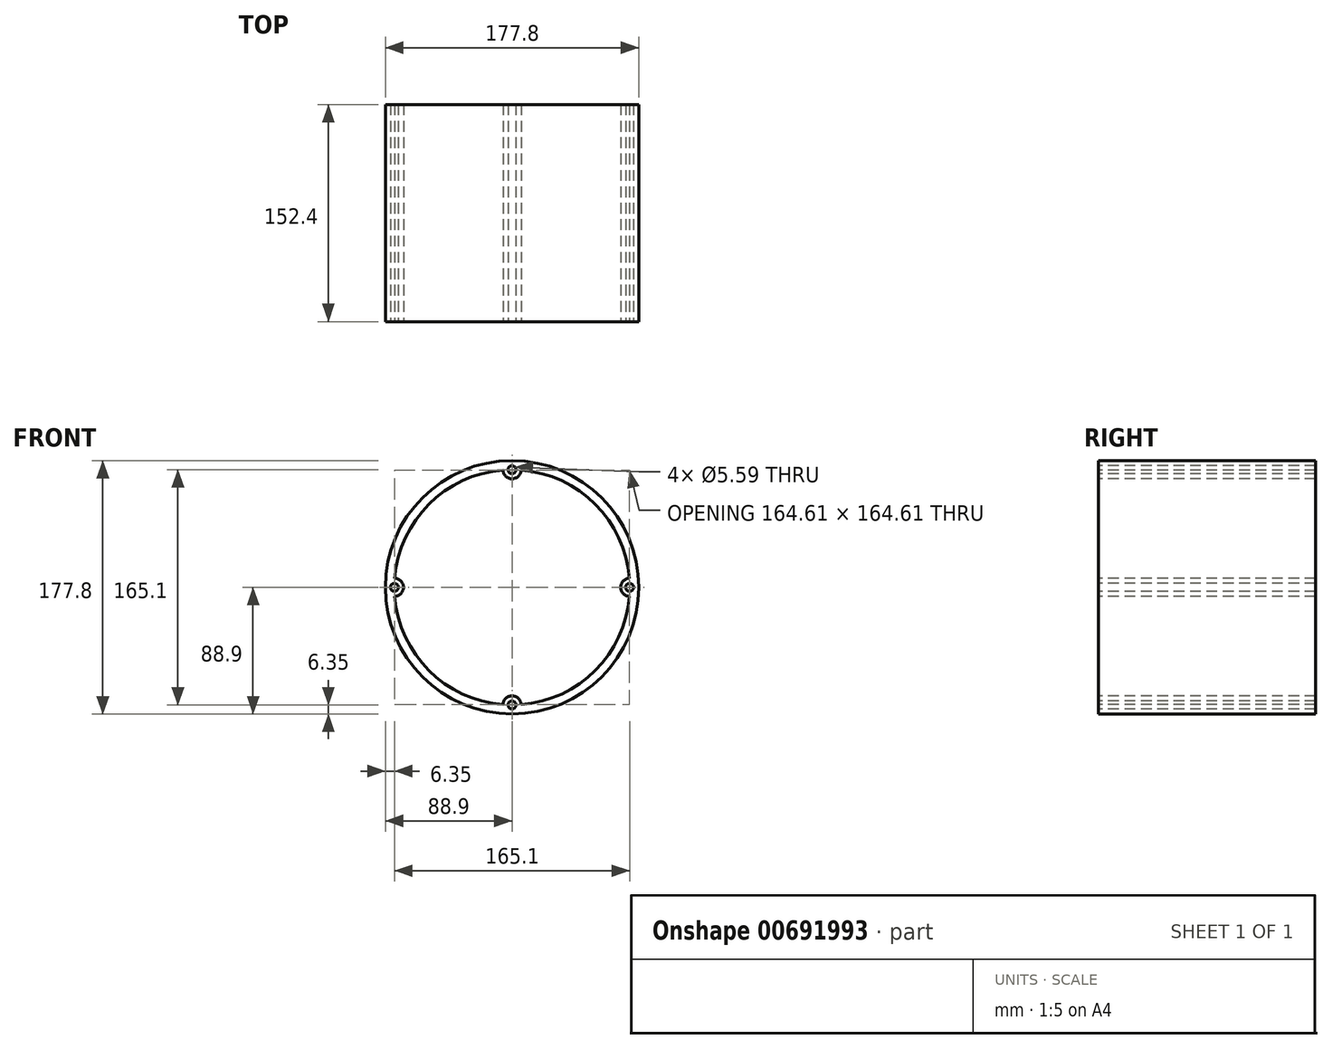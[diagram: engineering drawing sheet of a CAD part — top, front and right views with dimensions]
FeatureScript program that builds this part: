
annotation { "Feature Type Name" : "Feature", "Feature Type Description" : "" }
export const myFeature = defineFeature(function(context is Context, id is Id, definition is map)
    precondition{}
    {
        {
            var Q0;
            Q0=qCreatedBy(makeId("Front.planeOp"),FACE);
            var sketch = newSketch(context, id + "F0", { "sketchPlane" : qUnion([Q0])});
            skCircle(sketch, "E0", {"center": v(0, 0) * mm, "radius": 88.9 * mm});
            skSolve(sketch);
        }
        {
            var Q0;
            Q0=makeQuery(id+"F0.imprint","IMPRINT",FACE,{"disambiguationData":[TD([[makeQuery(id+"F0.imprint","IMPRINT",EDGE,{"derivedFrom":sQuery(id+"F0.wireOp",EDGE,"E0")}),1.0]])]});
            extrude(context, id + "F1", {"entities" : qUnion([Q0]), "oppositeDirection" : true, "depth" : 152.4 * mm, "offsetDistance" : 25.4 * mm});
        }
        {
            var Q0;
            Q0=makeQuery(id+"F1.opExtrude","CAP_FACE",FACE,{"disambiguationData":[OSD([sQuery(id+"F0.wireOp",EDGE,"E0")])],"isStart":true});
            var sketch = newSketch(context, id + "F2", { "sketchPlane" : qUnion([Q0])});
            skArc(sketch, "E1", {"start": v(2.8, -82.5) * mm, "mid": v(58.37, -58.37) * mm, "end": v(82.5, -2.8) * mm});
            skLineSegment(sketch, "E2", {"start": v(0, 0) * mm, "end": v(0, 79.76) * mm});
            skLineSegment(sketch, "E3", {"start": v(0, 0) * mm, "end": v(0, -79.76) * mm});
            skLineSegment(sketch, "E4", {"start": v(0, 0) * mm, "end": v(79.76, 0) * mm});
            skLineSegment(sketch, "E5", {"start": v(0, 0) * mm, "end": v(-79.76, 0) * mm});
            skCircle(sketch, "E6", {"center": v(0, 82.55) * mm, "radius": 2.8 * mm});
            skCircle(sketch, "E7", {"center": v(-82.55, 0) * mm, "radius": 2.8 * mm});
            skCircle(sketch, "E8", {"center": v(82.55, 0) * mm, "radius": 2.8 * mm});
            skCircle(sketch, "E9", {"center": v(0, -82.55) * mm, "radius": 2.8 * mm});
            skArc(sketch, "E10.trimOffspring", {"start": v(82.5, 2.8) * mm, "mid": v(58.37, 58.37) * mm, "end": v(2.8, 82.5) * mm});
            skArc(sketch, "E11.trimOffspring", {"start": v(-2.8, 82.5) * mm, "mid": v(-58.37, 58.37) * mm, "end": v(-82.5, 2.8) * mm});
            skArc(sketch, "E12.trimOffspring", {"start": v(-82.5, -2.8) * mm, "mid": v(-58.37, -58.37) * mm, "end": v(-2.8, -82.5) * mm});
            skSolve(sketch);
        }
        {
            var Q0;
            Q0=makeQuery(id+"F0.imprint","IMPRINT",FACE,{"disambiguationData":[TD([[makeQuery(id+"F0.imprint","IMPRINT",EDGE,{"derivedFrom":sQuery(id+"F0.wireOp",EDGE,"E0")}),1.0]])]});
            var sketch = newSketch(context, id + "F3", { "sketchPlane" : qUnion([Q0])});
            skCircle(sketch, "E13", {"center": v(0, 82.55) * mm, "radius": 6.35 * mm});
            skCircle(sketch, "E14", {"center": v(82.55, 0) * mm, "radius": 6.35 * mm});
            skCircle(sketch, "E15", {"center": v(-82.55, 0) * mm, "radius": 6.35 * mm});
            skCircle(sketch, "E16", {"center": v(0, -82.55) * mm, "radius": 6.35 * mm});
            skArc(sketch, "E17", {"start": v(-6.35, 82.3) * mm, "mid": v(-58.37, 58.37) * mm, "end": v(-82.3, 6.35) * mm});
            skArc(sketch, "E18.trimOffspring", {"start": v(82.3, 6.35) * mm, "mid": v(58.37, 58.37) * mm, "end": v(6.35, 82.3) * mm});
            skArc(sketch, "E19.trimOffspring", {"start": v(6.35, -82.3) * mm, "mid": v(58.37, -58.37) * mm, "end": v(82.3, -6.35) * mm});
            skArc(sketch, "E20.trimOffspring", {"start": v(-82.3, -6.35) * mm, "mid": v(-58.37, -58.37) * mm, "end": v(-6.35, -82.3) * mm});
            skSolve(sketch);
        }
        {
            var Q0;
            {var subQ0=sQuery(id+"F3.wireOp",EDGE,"E17");Q0=makeQuery(id+"F3.imprint","IMPRINT",FACE,{"disambiguationData":[TD([[makeQuery(id+"F3.imprint","IMPRINT",EDGE,{"derivedFrom":subQ0}),1.0]])]});}
            extrude(context, id + "F4", {"entities" : qUnion([Q0]), "operationType" : NewBodyOperationType.REMOVE, "endBound" : BoundingType.THROUGH_ALL, "oppositeDirection" : true, "depth" : 25.4 * mm, "offsetDistance" : 25.4 * mm});
        }
        {
            var Q0;
            {var subQ0=sQuery(id+"F2.wireOp",EDGE,"E6");var subQ1=makeQuery(id+"F2.imprint","INTERSECT",VERTEX,{"derivedFrom":[sQuery(id+"F2.wireOp",EDGE,"E2"),subQ0]});Q0=makeQuery(id+"F2.imprint","IMPRINT",FACE,{"disambiguationData":[TD([[makeQuery(id+"F2.imprint","IMPRINT",EDGE,{"disambiguationData":[TD([[subQ1,1.0]])],"derivedFrom":subQ0}),1.0]])]});}
            var Q1;
            {var subQ0=sQuery(id+"F2.wireOp",EDGE,"E7");var subQ1=makeQuery(id+"F2.imprint","INTERSECT",VERTEX,{"derivedFrom":[sQuery(id+"F2.wireOp",EDGE,"E5"),subQ0]});Q1=makeQuery(id+"F2.imprint","IMPRINT",FACE,{"disambiguationData":[TD([[makeQuery(id+"F2.imprint","IMPRINT",EDGE,{"disambiguationData":[TD([[subQ1,-1.0]])],"derivedFrom":subQ0}),1.0]])]});}
            var Q2;
            {var subQ0=sQuery(id+"F2.wireOp",EDGE,"E8");var subQ1=makeQuery(id+"F2.imprint","INTERSECT",VERTEX,{"derivedFrom":[sQuery(id+"F2.wireOp",EDGE,"E4"),subQ0]});Q2=makeQuery(id+"F2.imprint","IMPRINT",FACE,{"disambiguationData":[TD([[makeQuery(id+"F2.imprint","IMPRINT",EDGE,{"disambiguationData":[TD([[subQ1,1.0]])],"derivedFrom":subQ0}),1.0]])]});}
            var Q3;
            {var subQ0=sQuery(id+"F2.wireOp",EDGE,"E9");var subQ1=makeQuery(id+"F2.imprint","INTERSECT",VERTEX,{"derivedFrom":[sQuery(id+"F2.wireOp",EDGE,"E1"),subQ0]});Q3=makeQuery(id+"F2.imprint","IMPRINT",FACE,{"disambiguationData":[TD([[makeQuery(id+"F2.imprint","IMPRINT",EDGE,{"disambiguationData":[TD([[subQ1,-1.0]])],"derivedFrom":subQ0}),1.0]])]});}
            extrude(context, id + "F5", {"entities" : qUnion([Q0, Q1, Q2, Q3]), "operationType" : NewBodyOperationType.REMOVE, "endBound" : BoundingType.THROUGH_ALL, "oppositeDirection" : true, "depth" : 25.4 * mm, "offsetDistance" : 25.4 * mm});
        }
    });
